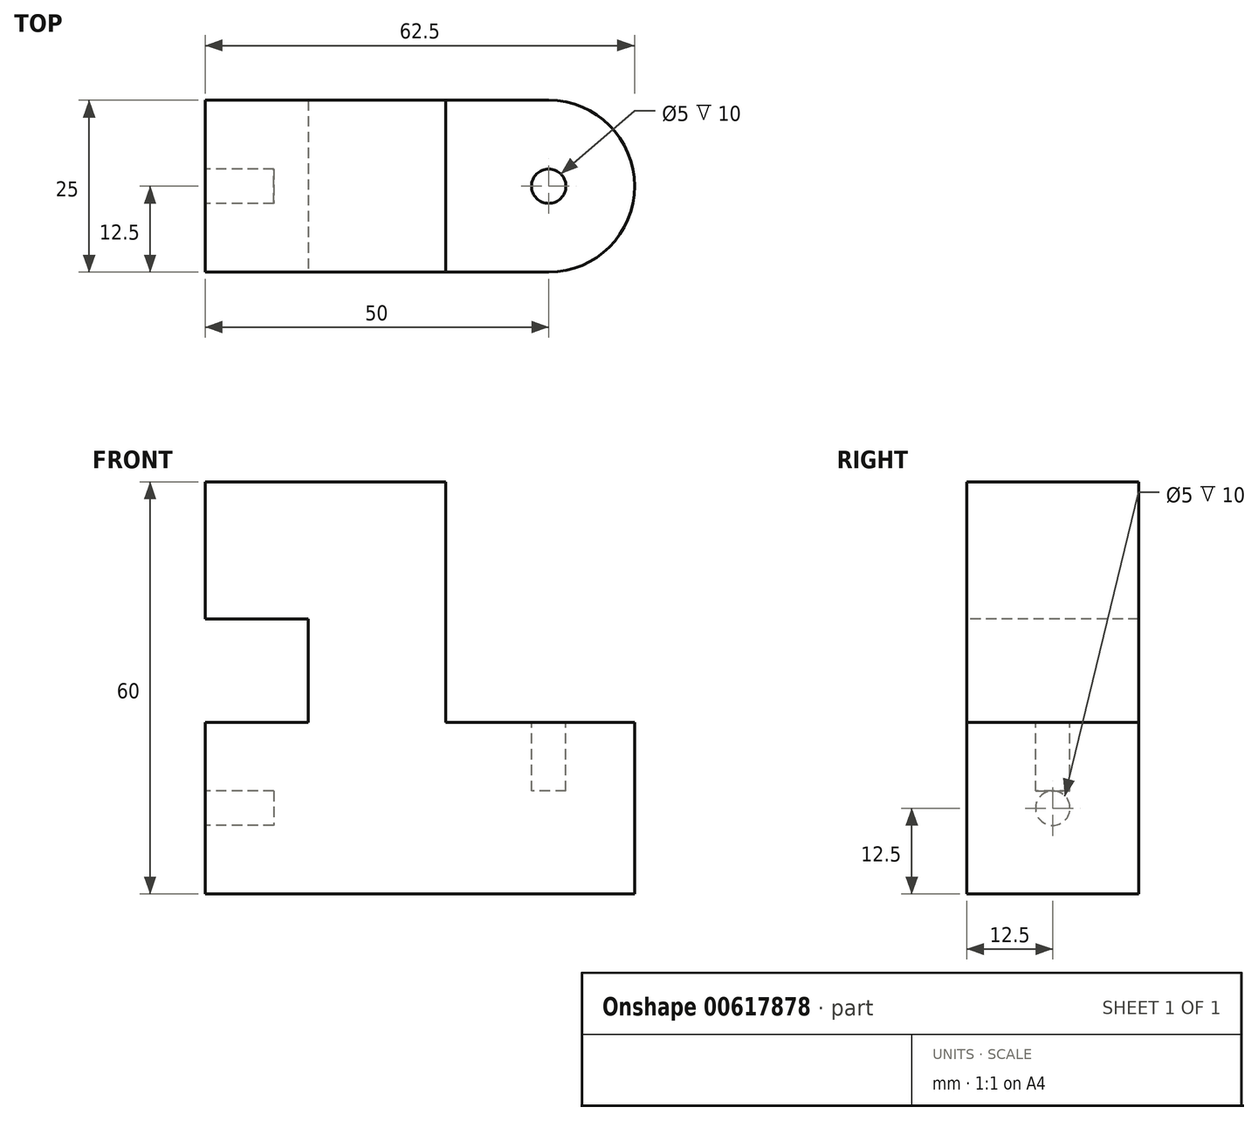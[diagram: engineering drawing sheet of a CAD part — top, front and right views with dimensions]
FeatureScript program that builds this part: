
annotation { "Feature Type Name" : "Feature", "Feature Type Description" : "" }
export const myFeature = defineFeature(function(context is Context, id is Id, definition is map)
    precondition{}
    {
        {
            var Q0;
            Q0=qCreatedBy(makeId("Top.planeOp"),FACE);
            var sketch = newSketch(context, id + "F0", { "sketchPlane" : qUnion([Q0])});
            skLineSegment(sketch, "E0.bottom", {"start": v(0, 0) * mm, "end": v(50, 0) * mm});
            skLineSegment(sketch, "E0.top", {"start": v(0, 25) * mm, "end": v(50, 25) * mm});
            skLineSegment(sketch, "E0.left", {"start": v(0, 0) * mm, "end": v(0, 25) * mm});
            skLineSegment(sketch, "E0.right", {"start": v(50, 0) * mm, "end": v(50, 0) * mm});
            skArc(sketch, "E1", {"start": v(50, 0) * mm, "mid": v(62.5, 12.5) * mm, "end": v(50, 25) * mm});
            skLineSegment(sketch, "E2.trimOffspring", {"start": v(50, 25) * mm, "end": v(50, 25) * mm});
            skSolve(sketch);
        }
        {
            var Q0;
            Q0=makeQuery(id+"F0.imprint","IMPRINT",FACE,{"disambiguationData":[TD([[makeQuery(id+"F0.imprint","IMPRINT",EDGE,{"derivedFrom":sQuery(id+"F0.wireOp",EDGE,"E0.bottom")}),1.0]])]});
            extrude(context, id + "F1", {"entities" : qUnion([Q0]), "depth" : 25 * mm, "offsetDistance" : 25 * mm});
        }
        {
            var Q0;
            Q0=makeQuery(id+"F1.opExtrude","CAP_FACE",FACE,{"disambiguationData":[OSD([sQuery(id+"F0.wireOp",EDGE,"E0.bottom"),sQuery(id+"F0.wireOp",EDGE,"E0.top"),sQuery(id+"F0.wireOp",EDGE,"E0.left"),sQuery(id+"F0.wireOp",EDGE,"E1")])],"isStart":false});
            var sketch = newSketch(context, id + "F2", { "sketchPlane" : qUnion([Q0])});
            skCircle(sketch, "E3", {"center": v(50, 12.5) * mm, "radius": 2.5 * mm});
            skSolve(sketch);
        }
        {
            var Q0;
            Q0 = qSketchRegion(id + "F2", true);
            extrude(context, id + "F3", {"entities" : qUnion([Q0]), "operationType" : NewBodyOperationType.REMOVE, "oppositeDirection" : true, "depth" : 10 * mm, "offsetDistance" : 25 * mm});
        }
        {
            var Q0;
            Q0=makeQuery(id+"F1.opExtrude","SWEPT_FACE",FACE,{"disambiguationData":[OSD([sQuery(id+"F0.wireOp",EDGE,"E0.left")])]});
            var sketch = newSketch(context, id + "F4", { "sketchPlane" : qUnion([Q0])});
            skPoint(sketch, "E4.endSnap0", {"position": v(-12.5, 0) * mm});
            skCircle(sketch, "E5", {"center": v(-12.5, 12.5) * mm, "radius": 2.5 * mm});
            skSolve(sketch);
        }
        {
            var Q0;
            Q0 = qSketchRegion(id + "F4", true);
            extrude(context, id + "F5", {"entities" : qUnion([Q0]), "operationType" : NewBodyOperationType.REMOVE, "oppositeDirection" : true, "depth" : 10 * mm, "offsetDistance" : 25 * mm});
        }
        {
            var Q0;
            Q0=makeQuery(id+"F1.opExtrude","SWEPT_FACE",FACE,{"disambiguationData":[OSD([sQuery(id+"F0.wireOp",EDGE,"E0.bottom")])]});
            var sketch = newSketch(context, id + "F6", { "sketchPlane" : qUnion([Q0])});
            skLineSegment(sketch, "E6", {"start": v(15, 25) * mm, "end": v(15, 40) * mm});
            skLineSegment(sketch, "E7", {"start": v(15, 40) * mm, "end": v(0, 40) * mm});
            skLineSegment(sketch, "E8", {"start": v(0, 40) * mm, "end": v(0, 60) * mm});
            skLineSegment(sketch, "E9", {"start": v(35, 60) * mm, "end": v(35, 25) * mm});
            skLineSegment(sketch, "E10", {"start": v(15, 25) * mm, "end": v(35, 25) * mm});
            skLineSegment(sketch, "E11", {"start": v(0, 60) * mm, "end": v(35, 60) * mm});
            skSolve(sketch);
        }
        {
            var Q0;
            Q0 = qSketchRegion(id + "F6", true);
            extrude(context, id + "F7", {"entities" : qUnion([Q0]), "operationType" : NewBodyOperationType.ADD, "oppositeDirection" : true, "depth" : 25 * mm, "offsetDistance" : 25 * mm});
        }
    });
